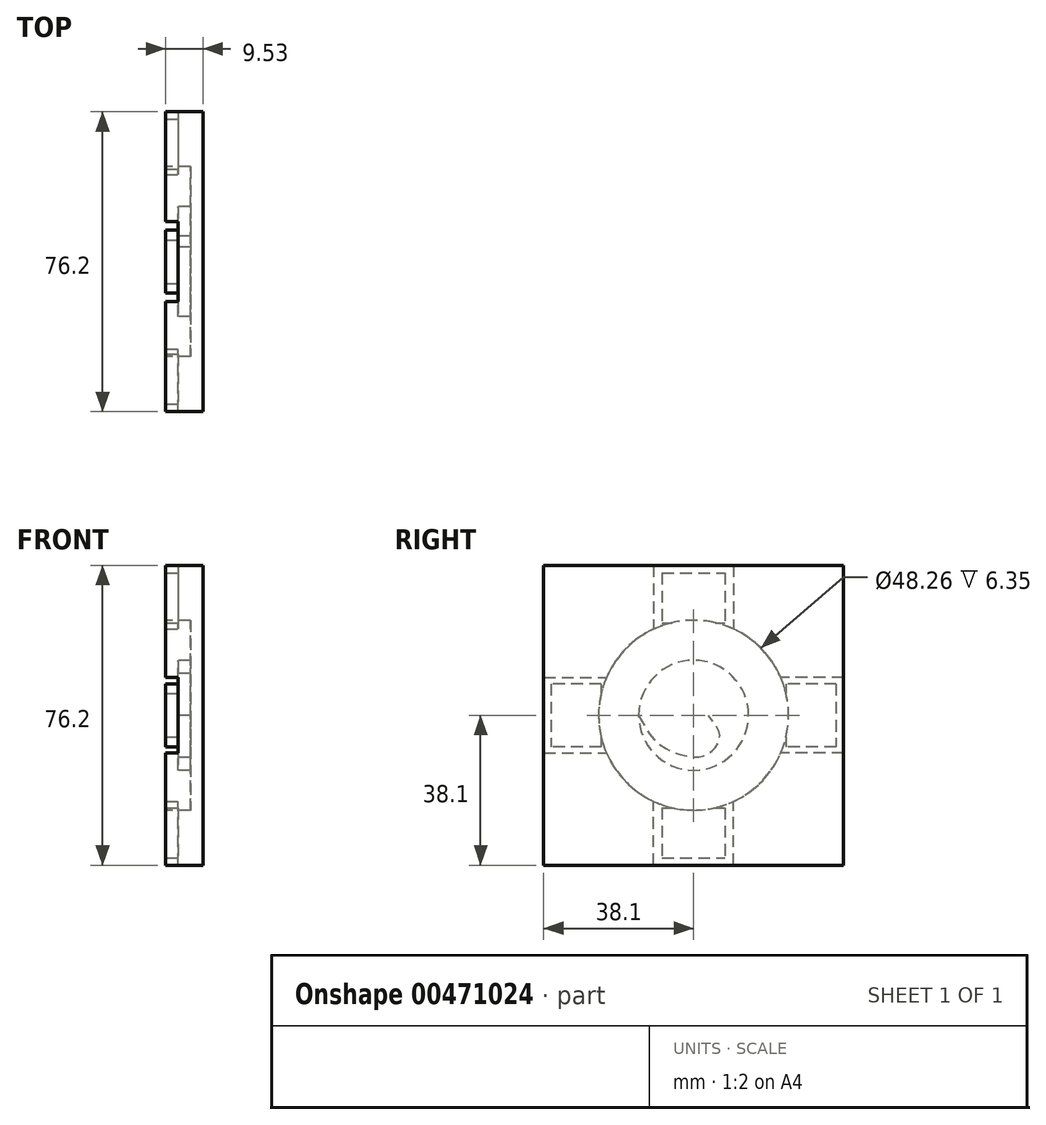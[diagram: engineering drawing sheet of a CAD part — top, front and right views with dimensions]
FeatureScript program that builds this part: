
annotation { "Feature Type Name" : "Feature", "Feature Type Description" : "" }
export const myFeature = defineFeature(function(context is Context, id is Id, definition is map)
    precondition{}
    {
        {
            var Q0;
            Q0=qCreatedBy(makeId("Right.planeOp"),FACE);
            var sketch = newSketch(context, id + "F0", { "sketchPlane" : qUnion([Q0])});
            skLineSegment(sketch, "E0.bottom", {"start": v(-38.1, 38.1) * mm, "end": v(38.1, 38.1) * mm});
            skLineSegment(sketch, "E0.top", {"start": v(-38.1, -38.1) * mm, "end": v(38.1, -38.1) * mm});
            skLineSegment(sketch, "E0.left", {"start": v(-38.1, 38.1) * mm, "end": v(-38.1, -38.1) * mm});
            skLineSegment(sketch, "E0.right", {"start": v(38.1, 38.1) * mm, "end": v(38.1, -38.1) * mm});
            skPoint(sketch, "E0.middle", {"position": v(0, 0) * mm});
            skCircle(sketch, "E1", {"center": v(0, 0) * mm, "radius": 13.97 * mm});
            skCircle(sketch, "E2.0", {"center": v(0, 0) * mm, "radius": 24.13 * mm});
            skSolve(sketch);
        }
        {
            var Q0;
            Q0=makeQuery(id+"F0.imprint","IMPRINT",FACE,{"disambiguationData":[TD([[makeQuery(id+"F0.imprint","IMPRINT",EDGE,{"derivedFrom":sQuery(id+"F0.wireOp",EDGE,"E0.bottom")}),-1.0]])]});
            var Q1;
            Q1=makeQuery(id+"F0.imprint","IMPRINT",FACE,{"disambiguationData":[TD([[makeQuery(id+"F0.imprint","IMPRINT",EDGE,{"derivedFrom":sQuery(id+"F0.wireOp",EDGE,"E1")}),-1.0]])]});
            var Q2;
            Q2=makeQuery(id+"F0.imprint","IMPRINT",FACE,{"disambiguationData":[TD([[makeQuery(id+"F0.imprint","IMPRINT",EDGE,{"derivedFrom":sQuery(id+"F0.wireOp",EDGE,"E1")}),1.0]])]});
            extrude(context, id + "F1", {"entities" : qUnion([Q0, Q1, Q2]), "depth" : 6.35 * mm});
        }
        {
            var Q0;
            Q0=makeQuery(id+"F0.imprint","IMPRINT",FACE,{"disambiguationData":[TD([[makeQuery(id+"F0.imprint","IMPRINT",EDGE,{"derivedFrom":sQuery(id+"F0.wireOp",EDGE,"E1")}),-1.0]])]});
            extrude(context, id + "F2", {"entities" : qUnion([Q0]), "operationType" : NewBodyOperationType.REMOVE, "depth" : 3.17 * mm});
        }
        {
            var Q0;
            Q0=makeQuery(id+"F0.imprint","IMPRINT",FACE,{"disambiguationData":[TD([[makeQuery(id+"F0.imprint","IMPRINT",EDGE,{"derivedFrom":sQuery(id+"F0.wireOp",EDGE,"E1")}),1.0]])]});
            var sketch = newSketch(context, id + "F3", { "sketchPlane" : qUnion([Q0])});
            skLineSegment(sketch, "E3", {"start": v(14.31, 0) * mm, "end": v(-13.96, 0) * mm});
            skFitSpline(sketch, "E4", {"points": [v(-13.96, 0) * mm, v(-8.66, -7.42) * mm, v(0, -10.6) * mm, v(4.06, -9.54) * mm, v(6.54, -6.36) * mm, v(6.18, -3.53) * mm, v(3.71, 0) * mm], "startDerivative": vector(19.34, -37.88) * mm, "endDerivative": vector(-19.2, 23.84) * mm});
            skFitSpline(sketch, "E5.MirrorCS", {"points": [v(-13.96, 0) * mm, v(-8.66, 7.42) * mm, v(0, 10.6) * mm, v(4.06, 9.54) * mm, v(6.54, 6.36) * mm, v(6.18, 3.53) * mm, v(3.71, 0) * mm], "startDerivative": vector(19.34, 37.88) * mm, "endDerivative": vector(-19.2, -23.84) * mm});
            skSolve(sketch);
        }
        {
            var Q0;
            Q0=makeQuery(id+"F0.imprint","IMPRINT",FACE,{"disambiguationData":[TD([[makeQuery(id+"F0.imprint","IMPRINT",EDGE,{"derivedFrom":sQuery(id+"F0.wireOp",EDGE,"E0.bottom")}),-1.0]])]});
            var sketch = newSketch(context, id + "F4", { "sketchPlane" : qUnion([Q0])});
            skLineSegment(sketch, "E6.0.0", {"start": v(-38.1, 38.1) * mm, "end": v(-38.1, 9.59) * mm});
            skLineSegment(sketch, "E6.0.1", {"start": v(-38.1, -38.1) * mm, "end": v(-10.16, -38.1) * mm});
            skLineSegment(sketch, "E6.0.2", {"start": v(38.1, -38.1) * mm, "end": v(38.1, -9.59) * mm});
            skLineSegment(sketch, "E6.0.3", {"start": v(38.1, 38.1) * mm, "end": v(10.16, 38.1) * mm});
            skArc(sketch, "E7.0", {"start": v(10.16, -21.89) * mm, "mid": v(17.28, -16.84) * mm, "end": v(22.14, -9.59) * mm});
            skLineSegment(sketch, "E8.bottom", {"start": v(38.1, -38.1) * mm, "end": v(10.16, -38.1) * mm});
            skLineSegment(sketch, "E8.top", {"start": v(38.1, -9.59) * mm, "end": v(22.14, -9.59) * mm});
            skLineSegment(sketch, "E8.right", {"start": v(10.16, -38.1) * mm, "end": v(10.16, -21.89) * mm});
            skLineSegment(sketch, "E9.top", {"start": v(-38.1, -9.59) * mm, "end": v(-22.14, -9.59) * mm});
            skLineSegment(sketch, "E9.left", {"start": v(-38.1, -38.1) * mm, "end": v(-38.1, -9.59) * mm});
            skLineSegment(sketch, "E9.right", {"start": v(-10.16, -38.1) * mm, "end": v(-10.16, -21.89) * mm});
            skLineSegment(sketch, "E10.bottom", {"start": v(-38.1, 38.1) * mm, "end": v(-10.16, 38.1) * mm});
            skLineSegment(sketch, "E10.top", {"start": v(-38.1, 9.59) * mm, "end": v(-22.14, 9.59) * mm});
            skLineSegment(sketch, "E10.right", {"start": v(-10.16, 38.1) * mm, "end": v(-10.16, 21.89) * mm});
            skLineSegment(sketch, "E11.top", {"start": v(38.1, 9.59) * mm, "end": v(22.14, 9.59) * mm});
            skLineSegment(sketch, "E11.left", {"start": v(38.1, 38.1) * mm, "end": v(38.1, 9.59) * mm});
            skLineSegment(sketch, "E11.right", {"start": v(10.16, 38.1) * mm, "end": v(10.16, 21.89) * mm});
            skPoint(sketch, "E12.orphan", {"position": v(10.16, -9.59) * mm});
            skPoint(sketch, "E13.orphan", {"position": v(-10.16, -9.59) * mm});
            skPoint(sketch, "E14.orphan", {"position": v(-10.16, 9.59) * mm});
            skPoint(sketch, "E15.orphan", {"position": v(10.16, 9.59) * mm});
            skLineSegment(sketch, "E16.bottom", {"start": v(36.2, 8) * mm, "end": v(23.5, 8) * mm});
            skLineSegment(sketch, "E16.top", {"start": v(36.2, -8) * mm, "end": v(23.5, -8) * mm});
            skLineSegment(sketch, "E16.left", {"start": v(36.2, 8) * mm, "end": v(36.2, -8) * mm});
            skLineSegment(sketch, "E16.right", {"start": v(-36.2, 8) * mm, "end": v(-36.2, -8) * mm});
            skLineSegment(sketch, "E17.bottom", {"start": v(-8, 36.2) * mm, "end": v(8, 36.2) * mm});
            skLineSegment(sketch, "E17.top", {"start": v(-8, -36.2) * mm, "end": v(8, -36.2) * mm});
            skLineSegment(sketch, "E17.left", {"start": v(-8, 36.2) * mm, "end": v(-8, 23.5) * mm});
            skLineSegment(sketch, "E17.right", {"start": v(8, 36.2) * mm, "end": v(8, 23.5) * mm});
            skLineSegment(sketch, "E18.0", {"start": v(23.5, 8) * mm, "end": v(23.5, 5.5) * mm});
            skLineSegment(sketch, "E19.0", {"start": v(-23.5, 8) * mm, "end": v(-23.5, 5.5) * mm});
            skLineSegment(sketch, "E20.0", {"start": v(-8, -23.5) * mm, "end": v(-5.5, -23.5) * mm});
            skLineSegment(sketch, "E21.0", {"start": v(-8, 23.5) * mm, "end": v(-5.5, 23.5) * mm});
            skLineSegment(sketch, "E22.trimOffspring", {"start": v(23.5, -5.5) * mm, "end": v(23.5, -8) * mm});
            skLineSegment(sketch, "E23.trimOffspring", {"start": v(5.5, 23.5) * mm, "end": v(8, 23.5) * mm});
            skLineSegment(sketch, "E24.trimOffspring", {"start": v(-23.5, -5.5) * mm, "end": v(-23.5, -8) * mm});
            skLineSegment(sketch, "E25.trimOffspring", {"start": v(5.5, -23.5) * mm, "end": v(8, -23.5) * mm});
            skLineSegment(sketch, "E26.trimOffspring", {"start": v(10.16, -38.1) * mm, "end": v(38.1, -38.1) * mm});
            skLineSegment(sketch, "E27.trimOffspring", {"start": v(8, -23.5) * mm, "end": v(8, -36.2) * mm});
            skArc(sketch, "E28.trimOffspring", {"start": v(-5.5, -23.5) * mm, "mid": v(0, -24.13) * mm, "end": v(5.5, -23.5) * mm});
            skLineSegment(sketch, "E29.trimOffspring", {"start": v(-8, -23.5) * mm, "end": v(-8, -36.2) * mm});
            skArc(sketch, "E30.trimOffspring", {"start": v(23.5, -5.5) * mm, "mid": v(24.13, 0) * mm, "end": v(23.5, 5.5) * mm});
            skLineSegment(sketch, "E31.trimOffspring", {"start": v(-23.5, -8) * mm, "end": v(-36.2, -8) * mm});
            skArc(sketch, "E32.trimOffspring", {"start": v(-22.14, -9.59) * mm, "mid": v(-17.28, -16.84) * mm, "end": v(-10.16, -21.89) * mm});
            skArc(sketch, "E33.trimOffspring", {"start": v(-23.5, 5.5) * mm, "mid": v(-24.13, 0) * mm, "end": v(-23.5, -5.5) * mm});
            skLineSegment(sketch, "E34.trimOffspring", {"start": v(-23.5, 8) * mm, "end": v(-36.2, 8) * mm});
            skArc(sketch, "E35.trimOffspring", {"start": v(22.14, 9.59) * mm, "mid": v(17.28, 16.84) * mm, "end": v(10.16, 21.89) * mm});
            skArc(sketch, "E36.trimOffspring", {"start": v(5.5, 23.5) * mm, "mid": v(0, 24.13) * mm, "end": v(-5.5, 23.5) * mm});
            skArc(sketch, "E37.trimOffspring", {"start": v(-10.16, 21.89) * mm, "mid": v(-17.28, 16.84) * mm, "end": v(-22.14, 9.59) * mm});
            skLineSegment(sketch, "E38.trimOffspring", {"start": v(-10.16, 38.1) * mm, "end": v(-38.1, 38.1) * mm});
            skLineSegment(sketch, "E39.trimOffspring", {"start": v(38.1, 9.59) * mm, "end": v(38.1, 38.1) * mm});
            skLineSegment(sketch, "E40.trimOffspring", {"start": v(-38.1, -9.59) * mm, "end": v(-38.1, -38.1) * mm});
            skSolve(sketch);
        }
        {
            var Q0;
            Q0 = qSketchRegion(id + "F4", true);
            extrude(context, id + "F5", {"entities" : qUnion([Q0]), "operationType" : NewBodyOperationType.ADD, "oppositeDirection" : true, "depth" : 3.17 * mm});
        }
        {
            var Q0;
            Q0 = qSketchRegion(id + "F3", true);
            extrude(context, id + "F6", {"entities" : qUnion([Q0]), "operationType" : NewBodyOperationType.REMOVE, "depth" : 3.17 * mm});
        }
    });
